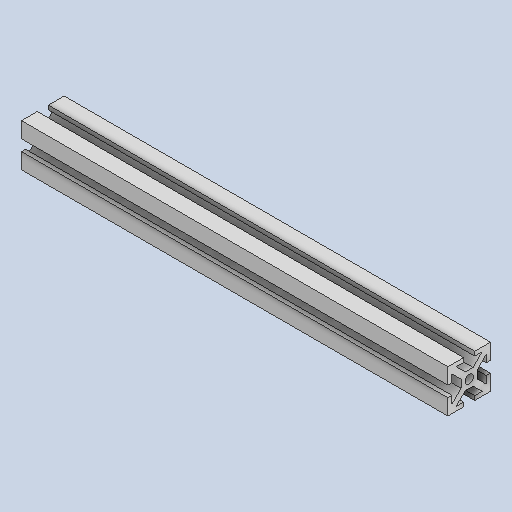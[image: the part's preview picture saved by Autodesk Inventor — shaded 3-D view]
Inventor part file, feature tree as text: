
AUTODESK INVENTOR PART (.ipt)
format: ipt  version: 2023 (Build 270158030, 158C)  size: 154,112 bytes
history: native  units: in
note: dims shown in document units (in); Inventor stores cm internally (conversion verified against a paired STEP export)
features: extrude x1, sketch x1
ambient origin geometry x8: Origin, YZ Plane, XZ Plane, XY Plane, X Axis, Y Axis, Z Axis, Center Point
bodies: Solid1 (feature_tree)
feature tree (2):
  extrude  "Extrusion1"  Depth=0.0975in
  sketch  "Sketch1"  dims[d2=0.37in d3=0.0975in d7=0.0975in d10=0.0975in d11=1.0in d13=0.0975in d16=0.0975in d17=0.37in d18=1.0in d23=0.0975in d24=1.0in d25=1.0in d32=0.175in d33=0.175in d35=135.0deg d36=0.175in d37=0.175in d38=0.0975in d40=0.175in d41=0.175in d42=0.175in d43=0.175in d44=0.2in d45=10.0in d46=0.0in]
